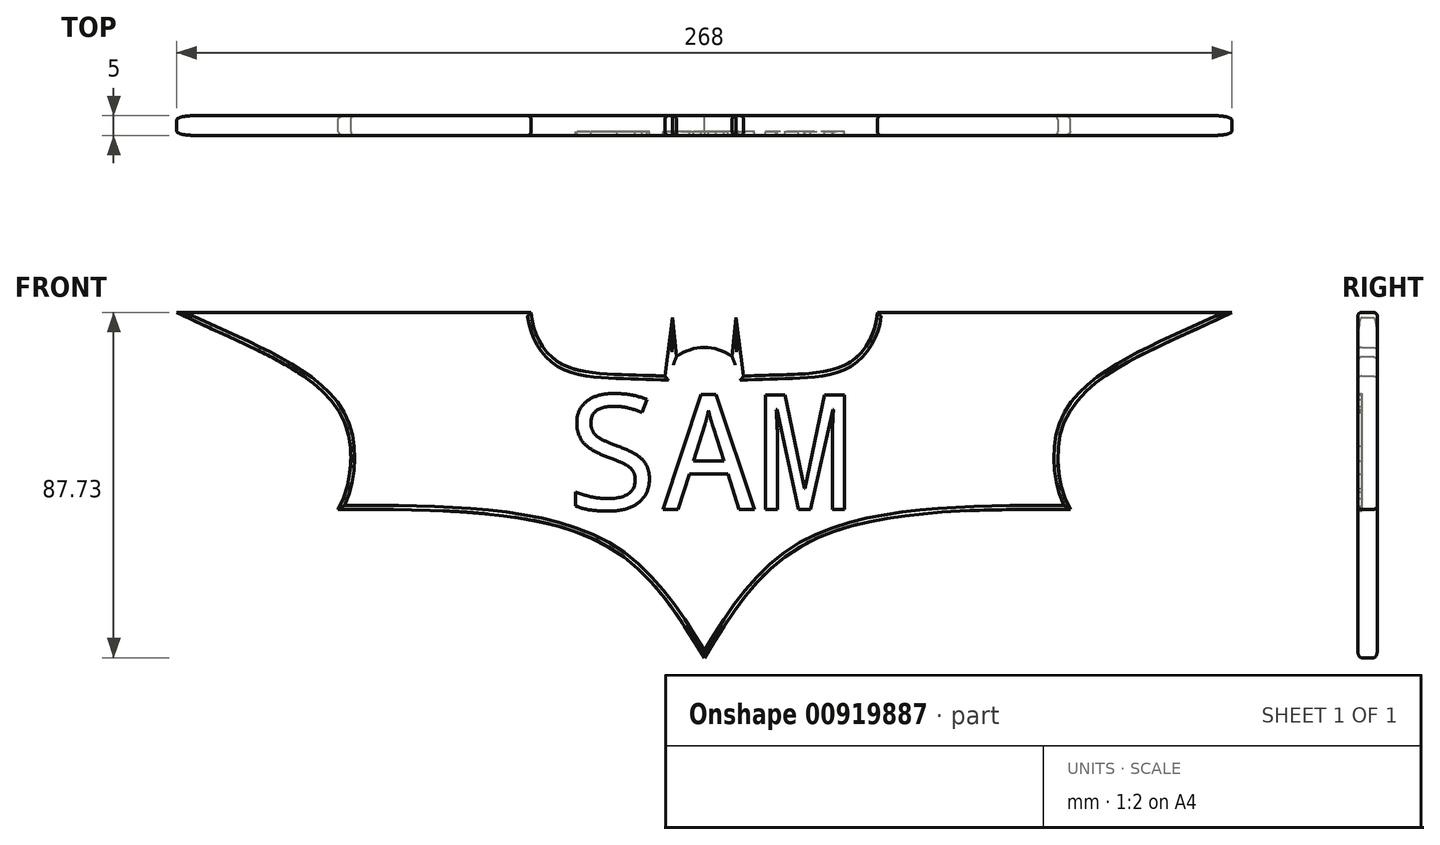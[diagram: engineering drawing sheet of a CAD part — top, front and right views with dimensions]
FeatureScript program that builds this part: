
annotation { "Feature Type Name" : "Feature", "Feature Type Description" : "" }
export const myFeature = defineFeature(function(context is Context, id is Id, definition is map)
    precondition{}
    {
        {
            var Q0;
            Q0=qCreatedBy(makeId("Front.planeOp"),FACE);
            var sketch = newSketch(context, id + "F0", { "sketchPlane" : qUnion([Q0])});
            skArc(sketch, "E0", {"start": v(7.06, 43.8) * mm, "mid": v(0, 46.17) * mm, "end": v(-7.06, 43.8) * mm});
            skLineSegment(sketch, "E1", {"start": v(-7.06, 43.8) * mm, "end": v(-8.09, 53.75) * mm});
            skLineSegment(sketch, "E2", {"start": v(-8.09, 53.75) * mm, "end": v(-10, 38.88) * mm});
            skFitSpline(sketch, "E3", {"points": [v(-10, 38.88) * mm, v(-36.7, 42.22) * mm, v(-44, 55.04) * mm], "startDerivative": vector(-67.87, 3.06) * mm, "endDerivative": vector(-3.47, 40.54) * mm});
            skLineSegment(sketch, "E4", {"start": v(-44, 55.04) * mm, "end": v(-134, 55.04) * mm});
            skFitSpline(sketch, "E5", {"points": [v(-134, 55.04) * mm, v(-92.16, 28.77) * mm, v(-93, 5.04) * mm], "startDerivative": vector(83.7, -40.96) * mm, "endDerivative": vector(-21.5, -36.05) * mm});
            skFitSpline(sketch, "E6", {"points": [v(-93, 5.04) * mm, v(-26.28, -3.43) * mm, v(0, -32.69) * mm], "startDerivative": vector(133.91, -0.06) * mm, "endDerivative": vector(48.28, -78.9) * mm});
            skFitSpline(sketch, "E7.MirrorCS", {"points": [v(93, 5.04) * mm, v(26.28, -3.43) * mm, v(0, -32.69) * mm], "startDerivative": vector(-133.91, -0.06) * mm, "endDerivative": vector(-48.28, -78.9) * mm});
            skFitSpline(sketch, "E8.MirrorCS", {"points": [v(134, 55.04) * mm, v(92.16, 28.77) * mm, v(93, 5.04) * mm], "startDerivative": vector(-83.7, -40.96) * mm, "endDerivative": vector(21.5, -36.05) * mm});
            skLineSegment(sketch, "E9.MirrorCS", {"start": v(44, 55.04) * mm, "end": v(134, 55.04) * mm});
            skFitSpline(sketch, "E10.MirrorCS", {"points": [v(10, 38.88) * mm, v(36.7, 42.22) * mm, v(44, 55.04) * mm], "startDerivative": vector(67.87, 3.06) * mm, "endDerivative": vector(3.47, 40.54) * mm});
            skLineSegment(sketch, "E11.MirrorCS", {"start": v(7.06, 43.8) * mm, "end": v(8.09, 53.75) * mm});
            skLineSegment(sketch, "E12.MirrorCS", {"start": v(8.09, 53.75) * mm, "end": v(10, 38.88) * mm});
            skSolve(sketch);
        }
        {
            var Q0;
            Q0=makeQuery(id+"F0.imprint","IMPRINT",FACE,{"disambiguationData":[TD([[makeQuery(id+"F0.imprint","IMPRINT",EDGE,{"derivedFrom":sQuery(id+"F0.wireOp",EDGE,"E0")}),1.0]])]});
            extrude(context, id + "F1", {"entities" : qUnion([Q0]), "depth" : 5 * mm});
        }
        {
            var Q0;
            Q0=qCreatedBy(makeId("Front.planeOp"),FACE);
            var sketch = newSketch(context, id + "F2", { "sketchPlane" : qUnion([Q0])});
            skText(sketch, "E13", { "text": "SAM", "fontName": "DroidSansMono.ttf"});
            const initialGuessF2  = {"E13": [-0.03558, 0.00496, 1, 0, 0.02935]};
            skSetInitialGuess(sketch, initialGuessF2);
            skSolve(sketch);
        }
        {
            var Q0;
            Q0=qSketchRegion(id+"F2",true);
            extrude(context, id + "F3", {"entities" : qUnion([Q0]), "operationType" : NewBodyOperationType.REMOVE, "depth" : 5 * mm, "hasSecondDirection" : true, "secondDirectionOppositeDirection" : false, "secondDirectionDepth" : 4 * mm});
        }
        {
            var Q0;
            Q0=makeQuery(id+"F1.opExtrude","CAP_EDGE",EDGE,{"disambiguationData":[OSD([sQuery(id+"F0.wireOp",EDGE,"E4")])],"isStart":false});
            var Q1;
            Q1=makeQuery(id+"F1.opExtrude","CAP_EDGE",EDGE,{"disambiguationData":[OSD([sQuery(id+"F0.wireOp",EDGE,"E5")])],"isStart":false});
            var Q2;
            Q2=makeQuery(id+"F1.opExtrude","CAP_EDGE",EDGE,{"disambiguationData":[OSD([sQuery(id+"F0.wireOp",EDGE,"E6")])],"isStart":false});
            var Q3;
            Q3=makeQuery(id+"F1.opExtrude","CAP_EDGE",EDGE,{"disambiguationData":[OSD([sQuery(id+"F0.wireOp",EDGE,"E7.MirrorCS")])],"isStart":false});
            var Q4;
            Q4=makeQuery(id+"F1.opExtrude","CAP_EDGE",EDGE,{"disambiguationData":[OSD([sQuery(id+"F0.wireOp",EDGE,"E8.MirrorCS")])],"isStart":false});
            var Q5;
            Q5=makeQuery(id+"F1.opExtrude","CAP_EDGE",EDGE,{"disambiguationData":[OSD([sQuery(id+"F0.wireOp",EDGE,"E9.MirrorCS")])],"isStart":false});
            var Q6;
            Q6=makeQuery(id+"F1.opExtrude","CAP_EDGE",EDGE,{"disambiguationData":[OSD([sQuery(id+"F0.wireOp",EDGE,"E11.MirrorCS")])],"isStart":false});
            var Q7;
            Q7=makeQuery(id+"F1.opExtrude","CAP_EDGE",EDGE,{"disambiguationData":[OSD([sQuery(id+"F0.wireOp",EDGE,"E1")])],"isStart":false});
            var Q8;
            Q8=makeQuery(id+"F1.opExtrude","CAP_EDGE",EDGE,{"disambiguationData":[OSD([sQuery(id+"F0.wireOp",EDGE,"E0")])],"isStart":false});
            var Q9;
            Q9=makeQuery(id+"F1.opExtrude","CAP_EDGE",EDGE,{"disambiguationData":[OSD([sQuery(id+"F0.wireOp",EDGE,"E2")])],"isStart":false});
            var Q10;
            Q10=makeQuery(id+"F1.opExtrude","CAP_EDGE",EDGE,{"disambiguationData":[OSD([sQuery(id+"F0.wireOp",EDGE,"E12.MirrorCS")])],"isStart":false});
            var Q11;
            Q11=makeQuery(id+"F1.opExtrude","CAP_EDGE",EDGE,{"disambiguationData":[OSD([sQuery(id+"F0.wireOp",EDGE,"E10.MirrorCS")])],"isStart":false});
            var Q12;
            Q12=makeQuery(id+"F1.opExtrude","CAP_EDGE",EDGE,{"disambiguationData":[OSD([sQuery(id+"F0.wireOp",EDGE,"E3")])],"isStart":false});
            var Q13;
            Q13=makeQuery(id+"F1.opExtrude","CAP_EDGE",EDGE,{"disambiguationData":[OSD([sQuery(id+"F0.wireOp",EDGE,"E12.MirrorCS")])],"isStart":true});
            var Q14;
            Q14=makeQuery(id+"F1.opExtrude","CAP_EDGE",EDGE,{"disambiguationData":[OSD([sQuery(id+"F0.wireOp",EDGE,"E11.MirrorCS")])],"isStart":true});
            var Q15;
            Q15=makeQuery(id+"F1.opExtrude","CAP_EDGE",EDGE,{"disambiguationData":[OSD([sQuery(id+"F0.wireOp",EDGE,"E0")])],"isStart":true});
            var Q16;
            Q16=makeQuery(id+"F1.opExtrude","CAP_EDGE",EDGE,{"disambiguationData":[OSD([sQuery(id+"F0.wireOp",EDGE,"E1")])],"isStart":true});
            var Q17;
            Q17=makeQuery(id+"F1.opExtrude","CAP_EDGE",EDGE,{"disambiguationData":[OSD([sQuery(id+"F0.wireOp",EDGE,"E2")])],"isStart":true});
            var Q18;
            Q18=makeQuery(id+"F1.opExtrude","CAP_EDGE",EDGE,{"disambiguationData":[OSD([sQuery(id+"F0.wireOp",EDGE,"E3")])],"isStart":true});
            var Q19;
            Q19=makeQuery(id+"F1.opExtrude","CAP_EDGE",EDGE,{"disambiguationData":[OSD([sQuery(id+"F0.wireOp",EDGE,"E10.MirrorCS")])],"isStart":true});
            var Q20;
            Q20=makeQuery(id+"F1.opExtrude","CAP_EDGE",EDGE,{"disambiguationData":[OSD([sQuery(id+"F0.wireOp",EDGE,"E9.MirrorCS")])],"isStart":true});
            var Q21;
            Q21=makeQuery(id+"F1.opExtrude","CAP_EDGE",EDGE,{"disambiguationData":[OSD([sQuery(id+"F0.wireOp",EDGE,"E8.MirrorCS")])],"isStart":true});
            var Q22;
            Q22=makeQuery(id+"F1.opExtrude","CAP_EDGE",EDGE,{"disambiguationData":[OSD([sQuery(id+"F0.wireOp",EDGE,"E7.MirrorCS")])],"isStart":true});
            var Q23;
            Q23=makeQuery(id+"F1.opExtrude","CAP_EDGE",EDGE,{"disambiguationData":[OSD([sQuery(id+"F0.wireOp",EDGE,"E6")])],"isStart":true});
            var Q24;
            Q24=makeQuery(id+"F1.opExtrude","CAP_EDGE",EDGE,{"disambiguationData":[OSD([sQuery(id+"F0.wireOp",EDGE,"E5")])],"isStart":true});
            var Q25;
            Q25=makeQuery(id+"F1.opExtrude","CAP_EDGE",EDGE,{"disambiguationData":[OSD([sQuery(id+"F0.wireOp",EDGE,"E4")])],"isStart":true});
            fillet(context, id + "F4", {"entities" : qUnion([Q0, Q1, Q2, Q3, Q4, Q5, Q6, Q7, Q8, Q9, Q10, Q11, Q12, Q13, Q14, Q15, Q16, Q17, Q18, Q19, Q20, Q21, Q22, Q23, Q24, Q25]), "radius" : 1 * mm, "tangentPropagation" : true, "allowEdgeOverflow" : false});
        }
    });
